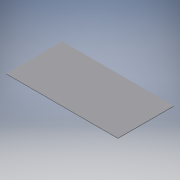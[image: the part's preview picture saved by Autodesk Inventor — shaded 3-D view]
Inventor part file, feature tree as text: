
AUTODESK INVENTOR PART (.ipt)
format: ipt  version: 2016 (Build 200138000, 138)  size: 94,720 bytes
history: native  units: mm
features: extrude x1, sketch x1
ambient origin geometry x8: Origin, YZ Plane, XZ Plane, XY Plane, X Axis, Y Axis, Z Axis, Center Point
bodies: Solid1 (feature_tree)
feature tree (2):
  extrude  "Extrusion1"  [1 undecoded]
  sketch  "Sketch1"  dims[d4=0.0mm]
note: 1 required parameter value undecoded (feature->parameter linkage not recoverable at this tier; creation-order binding heuristic only, values carry confidence <= 0.55)
